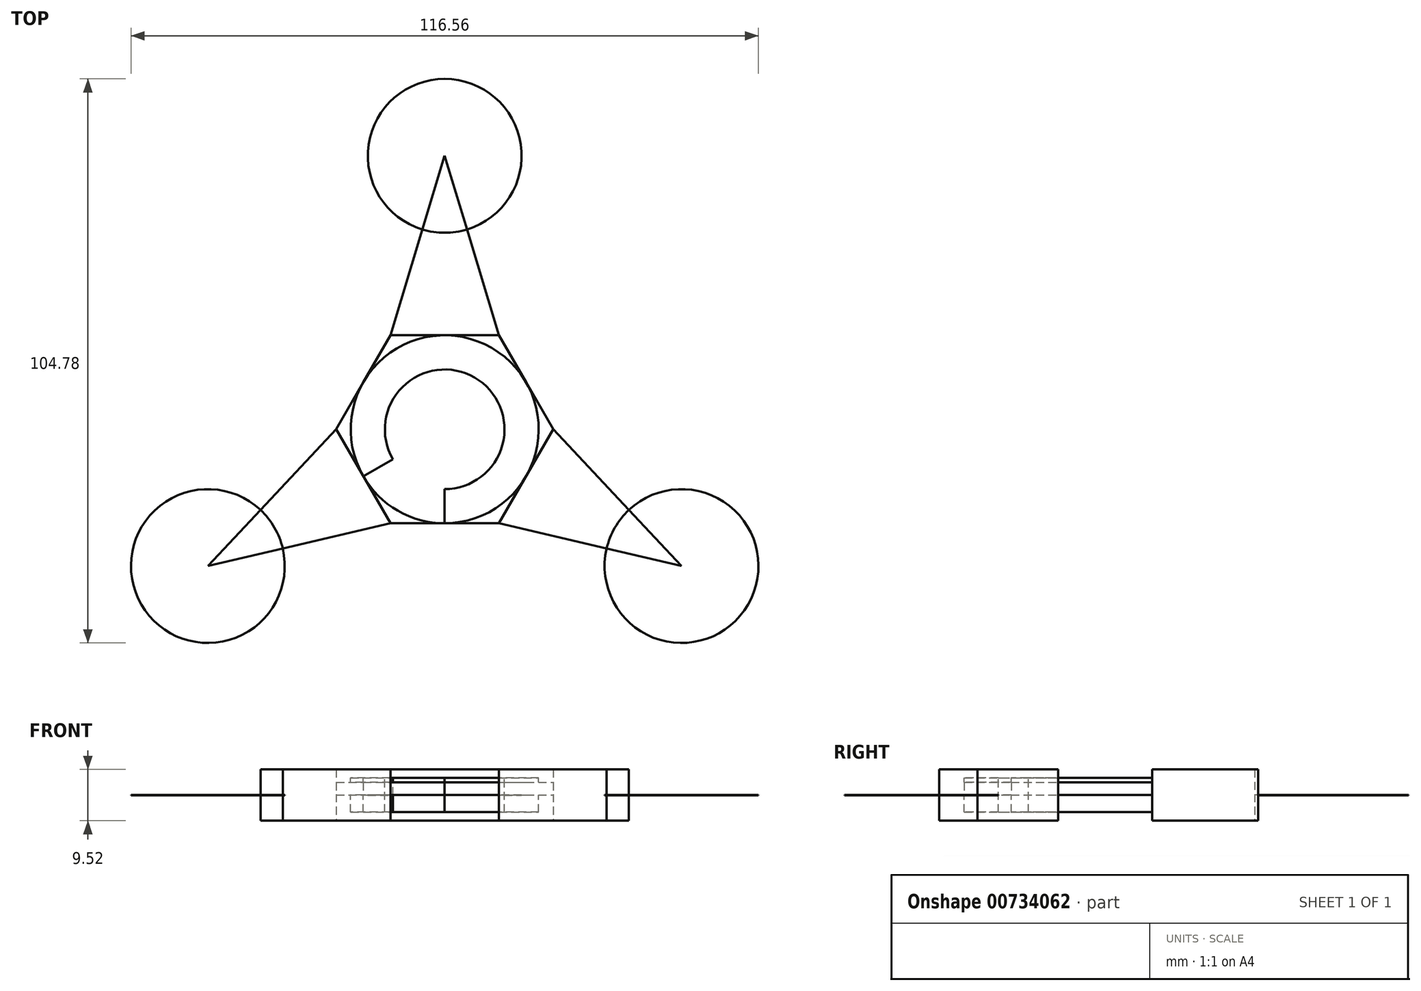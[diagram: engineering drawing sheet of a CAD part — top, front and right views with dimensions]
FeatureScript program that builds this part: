
annotation { "Feature Type Name" : "Feature", "Feature Type Description" : "" }
export const myFeature = defineFeature(function(context is Context, id is Id, definition is map)
    precondition{}
    {
        {
            var Q0;
            Q0=qCreatedBy(makeId("Top.planeOp"),FACE);
            var sketch = newSketch(context, id + "F0", { "sketchPlane" : qUnion([Q0])});
            skCircle(sketch, "E0", {"center": v(0, 0) * mm, "radius": 11.11 * mm});
            skCircle(sketch, "E1", {"center": v(0, 0) * mm, "radius": 17.46 * mm});
            skPoint(sketch, "E2.0.midPoint", {"position": v(15.12, 8.73) * mm});
            skCircle(sketch, "E3.cCircle", {"center": v(0, 0) * mm, "radius": 17.46 * mm, "construction": true});
            skLineSegment(sketch, "E3.0", {"start": v(10.08, 17.46) * mm, "end": v(20.16, 0) * mm});
            skLineSegment(sketch, "E3.1", {"start": v(20.16, 0) * mm, "end": v(10.08, -17.46) * mm});
            skLineSegment(sketch, "E3.2", {"start": v(10.08, -17.46) * mm, "end": v(-10.08, -17.46) * mm});
            skLineSegment(sketch, "E3.3", {"start": v(-10.08, -17.46) * mm, "end": v(-20.16, 0) * mm});
            skLineSegment(sketch, "E3.4", {"start": v(-20.16, 0) * mm, "end": v(-10.08, 17.46) * mm});
            skLineSegment(sketch, "E3.5", {"start": v(-10.08, 17.46) * mm, "end": v(10.08, 17.46) * mm});
            skLineSegment(sketch, "E4", {"start": v(-10.08, 17.46) * mm, "end": v(0, 50.8) * mm});
            skLineSegment(sketch, "E5", {"start": v(0, 50.8) * mm, "end": v(10.08, 17.46) * mm});
            skLineSegment(sketch, "E6", {"start": v(0, 50.8) * mm, "end": v(0, -50.8) * mm});
            skLineSegment(sketch, "E7", {"start": v(-20.16, 0) * mm, "end": v(-44, -25.4) * mm});
            skLineSegment(sketch, "E8", {"start": v(-44, -25.4) * mm, "end": v(-10.08, -17.46) * mm});
            skLineSegment(sketch, "E9", {"start": v(-44, -25.4) * mm, "end": v(44, 25.4) * mm});
            skLineSegment(sketch, "E10", {"start": v(10.08, -17.46) * mm, "end": v(44, -25.4) * mm});
            skLineSegment(sketch, "E11", {"start": v(44, -25.4) * mm, "end": v(20.16, 0) * mm});
            skLineSegment(sketch, "E12", {"start": v(44, -25.4) * mm, "end": v(-44, 25.4) * mm});
            skCircle(sketch, "E13", {"center": v(-44, -25.4) * mm, "radius": 14.29 * mm});
            skCircle(sketch, "E14", {"center": v(44, -25.4) * mm, "radius": 14.29 * mm});
            skCircle(sketch, "E15", {"center": v(0, 50.8) * mm, "radius": 14.29 * mm});
            skSolve(sketch);
        }
        {
            var Q0;
            {var subQ0=sQuery(id+"F0.wireOp",EDGE,"E9");var subQ1=sQuery(id+"F0.wireOp",EDGE,"E0");var subQ2=makeQuery(id+"F0.imprint","INTERSECT",VERTEX,{"disambiguationData":[OD(1.0)],"derivedFrom":[subQ1,subQ0]});Q0=makeQuery(id+"F0.imprint","IMPRINT",FACE,{"disambiguationData":[TD([[makeQuery(id+"F0.imprint","IMPRINT",EDGE,{"disambiguationData":[TD([[subQ2,-1.0]])],"derivedFrom":subQ1}),-1.0]])]});}
            var Q1;
            {var subQ0=sQuery(id+"F0.wireOp",EDGE,"E6");var subQ1=sQuery(id+"F0.wireOp",EDGE,"E0");var subQ2=makeQuery(id+"F0.imprint","INTERSECT",VERTEX,{"disambiguationData":[OD(0.0)],"derivedFrom":[subQ1,subQ0]});Q1=makeQuery(id+"F0.imprint","IMPRINT",FACE,{"disambiguationData":[TD([[makeQuery(id+"F0.imprint","IMPRINT",EDGE,{"disambiguationData":[TD([[subQ2,-1.0]])],"derivedFrom":subQ1}),-1.0]])]});}
            var Q2;
            {var subQ0=sQuery(id+"F0.wireOp",EDGE,"E12");var subQ1=sQuery(id+"F0.wireOp",EDGE,"E0");var subQ2=makeQuery(id+"F0.imprint","INTERSECT",VERTEX,{"disambiguationData":[OD(0.0)],"derivedFrom":[subQ1,subQ0]});Q2=makeQuery(id+"F0.imprint","IMPRINT",FACE,{"disambiguationData":[TD([[makeQuery(id+"F0.imprint","IMPRINT",EDGE,{"disambiguationData":[TD([[subQ2,-1.0]])],"derivedFrom":subQ1}),-1.0]])]});}
            var Q3;
            {var subQ0=sQuery(id+"F0.wireOp",EDGE,"E6");var subQ1=sQuery(id+"F0.wireOp",EDGE,"E0");var subQ2=makeQuery(id+"F0.imprint","INTERSECT",VERTEX,{"disambiguationData":[OD(0.0)],"derivedFrom":[subQ1,subQ0]});Q3=makeQuery(id+"F0.imprint","IMPRINT",FACE,{"disambiguationData":[TD([[makeQuery(id+"F0.imprint","IMPRINT",EDGE,{"disambiguationData":[TD([[subQ2,1.0]])],"derivedFrom":subQ1}),-1.0]])]});}
            var Q4;
            {var subQ0=sQuery(id+"F0.wireOp",EDGE,"E9");var subQ1=sQuery(id+"F0.wireOp",EDGE,"E0");var subQ2=makeQuery(id+"F0.imprint","INTERSECT",VERTEX,{"disambiguationData":[OD(0.0)],"derivedFrom":[subQ1,subQ0]});Q4=makeQuery(id+"F0.imprint","IMPRINT",FACE,{"disambiguationData":[TD([[makeQuery(id+"F0.imprint","IMPRINT",EDGE,{"disambiguationData":[TD([[subQ2,1.0]])],"derivedFrom":subQ1}),-1.0]])]});}
            var Q5;
            {var subQ0=sQuery(id+"F0.wireOp",EDGE,"E6");var subQ1=sQuery(id+"F0.wireOp",EDGE,"E0");var subQ2=makeQuery(id+"F0.imprint","INTERSECT",VERTEX,{"disambiguationData":[OD(1.0)],"derivedFrom":[subQ1,subQ0]});Q5=makeQuery(id+"F0.imprint","IMPRINT",FACE,{"disambiguationData":[TD([[makeQuery(id+"F0.imprint","IMPRINT",EDGE,{"disambiguationData":[TD([[subQ2,-1.0]])],"derivedFrom":subQ1}),-1.0]])]});}
            extrude(context, id + "F1", {"entities" : qUnion([Q0, Q1, Q2, Q3, Q4, Q5]), "oppositeDirection" : true, "depth" : 3.17 * mm, "offsetDistance" : 25.4 * mm, "hasSecondDirection" : true, "secondDirectionOppositeDirection" : false, "secondDirectionDepth" : 3.17 * mm});
        }
        {
            var Q0;
            {var subQ0=sQuery(id+"F0.wireOp",EDGE,"E3.4");var subQ1=sQuery(id+"F0.wireOp",EDGE,"E1");var subQ2=makeQuery(id+"F0.imprint","INTERSECT",VERTEX,{"derivedFrom":[subQ1,subQ0,sQuery(id+"F0.wireOp",EDGE,"E12")]});Q0=makeQuery(id+"F0.imprint","IMPRINT",FACE,{"disambiguationData":[TD([[makeQuery(id+"F0.imprint","IMPRINT",EDGE,{"disambiguationData":[TD([[subQ2,-1.0]])],"derivedFrom":subQ1}),-1.0]])]});}
            var Q1;
            {var subQ0=sQuery(id+"F0.wireOp",EDGE,"E3.2");var subQ1=sQuery(id+"F0.wireOp",EDGE,"E1");var subQ2=makeQuery(id+"F0.imprint","INTERSECT",VERTEX,{"derivedFrom":[subQ1,subQ0,sQuery(id+"F0.wireOp",EDGE,"E6")]});Q1=makeQuery(id+"F0.imprint","IMPRINT",FACE,{"disambiguationData":[TD([[makeQuery(id+"F0.imprint","IMPRINT",EDGE,{"disambiguationData":[TD([[subQ2,1.0]])],"derivedFrom":subQ1}),-1.0]])]});}
            var Q2;
            {var subQ0=sQuery(id+"F0.wireOp",EDGE,"E3.4");var subQ1=sQuery(id+"F0.wireOp",EDGE,"E1");var subQ2=makeQuery(id+"F0.imprint","INTERSECT",VERTEX,{"derivedFrom":[subQ1,subQ0,sQuery(id+"F0.wireOp",EDGE,"E12")]});Q2=makeQuery(id+"F0.imprint","IMPRINT",FACE,{"disambiguationData":[TD([[makeQuery(id+"F0.imprint","IMPRINT",EDGE,{"disambiguationData":[TD([[subQ2,1.0]])],"derivedFrom":subQ1}),-1.0]])]});}
            var Q3;
            {var subQ0=sQuery(id+"F0.wireOp",EDGE,"E3.0");var subQ1=sQuery(id+"F0.wireOp",EDGE,"E1");var subQ2=makeQuery(id+"F0.imprint","INTERSECT",VERTEX,{"derivedFrom":[subQ1,subQ0,sQuery(id+"F0.wireOp",EDGE,"E9")]});Q3=makeQuery(id+"F0.imprint","IMPRINT",FACE,{"disambiguationData":[TD([[makeQuery(id+"F0.imprint","IMPRINT",EDGE,{"disambiguationData":[TD([[subQ2,-1.0]])],"derivedFrom":subQ1}),-1.0]])]});}
            var Q4;
            {var subQ0=sQuery(id+"F0.wireOp",EDGE,"E3.2");var subQ1=sQuery(id+"F0.wireOp",EDGE,"E1");var subQ2=makeQuery(id+"F0.imprint","INTERSECT",VERTEX,{"derivedFrom":[subQ1,subQ0,sQuery(id+"F0.wireOp",EDGE,"E6")]});Q4=makeQuery(id+"F0.imprint","IMPRINT",FACE,{"disambiguationData":[TD([[makeQuery(id+"F0.imprint","IMPRINT",EDGE,{"disambiguationData":[TD([[subQ2,-1.0]])],"derivedFrom":subQ1}),-1.0]])]});}
            var Q5;
            {var subQ0=sQuery(id+"F0.wireOp",EDGE,"E3.0");var subQ1=sQuery(id+"F0.wireOp",EDGE,"E1");var subQ2=makeQuery(id+"F0.imprint","INTERSECT",VERTEX,{"derivedFrom":[subQ1,subQ0,sQuery(id+"F0.wireOp",EDGE,"E9")]});Q5=makeQuery(id+"F0.imprint","IMPRINT",FACE,{"disambiguationData":[TD([[makeQuery(id+"F0.imprint","IMPRINT",EDGE,{"disambiguationData":[TD([[subQ2,1.0]])],"derivedFrom":subQ1}),-1.0]])]});}
            extrude(context, id + "F2", {"entities" : qUnion([Q0, Q1, Q2, Q3, Q4, Q5]), "operationType" : NewBodyOperationType.ADD, "depth" : 2.38 * mm, "offsetDistance" : 25.4 * mm, "hasSecondDirection" : true, "secondDirectionOppositeDirection" : true, "secondDirectionDepth" : 3 / 812.8 * mm});
        }
        {
            var Q0;
            {var subQ0=sQuery(id+"F0.wireOp",EDGE,"E10");var subQ5=sQuery(id+"F0.wireOp",EDGE,"E14");var subQ6=makeQuery(id+"F0.imprint","INTERSECT",VERTEX,{"derivedFrom":[subQ0,subQ5]});Q0=makeQuery(id+"F0.imprint","IMPRINT",FACE,{"disambiguationData":[TD([[makeQuery(id+"F0.imprint","IMPRINT",EDGE,{"disambiguationData":[TD([[subQ6,1.0]])],"derivedFrom":subQ5}),-1.0]])]});}
            var Q1;
            {var subQ0=sQuery(id+"F0.wireOp",EDGE,"E11");var subQ5=sQuery(id+"F0.wireOp",EDGE,"E14");var subQ7=makeQuery(id+"F0.imprint","INTERSECT",VERTEX,{"derivedFrom":[subQ0,subQ5]});Q1=makeQuery(id+"F0.imprint","IMPRINT",FACE,{"disambiguationData":[TD([[makeQuery(id+"F0.imprint","IMPRINT",EDGE,{"disambiguationData":[TD([[subQ7,-1.0]])],"derivedFrom":subQ5}),-1.0]])]});}
            var Q2;
            {var subQ0=sQuery(id+"F0.wireOp",EDGE,"E5");var subQ5=sQuery(id+"F0.wireOp",EDGE,"E15");var subQ6=makeQuery(id+"F0.imprint","INTERSECT",VERTEX,{"derivedFrom":[subQ0,subQ5]});Q2=makeQuery(id+"F0.imprint","IMPRINT",FACE,{"disambiguationData":[TD([[makeQuery(id+"F0.imprint","IMPRINT",EDGE,{"disambiguationData":[TD([[subQ6,1.0]])],"derivedFrom":subQ5}),-1.0]])]});}
            var Q3;
            {var subQ0=sQuery(id+"F0.wireOp",EDGE,"E4");var subQ5=sQuery(id+"F0.wireOp",EDGE,"E15");var subQ6=makeQuery(id+"F0.imprint","INTERSECT",VERTEX,{"derivedFrom":[subQ0,subQ5]});Q3=makeQuery(id+"F0.imprint","IMPRINT",FACE,{"disambiguationData":[TD([[makeQuery(id+"F0.imprint","IMPRINT",EDGE,{"disambiguationData":[TD([[subQ6,-1.0]])],"derivedFrom":subQ5}),-1.0]])]});}
            var Q4;
            {var subQ0=sQuery(id+"F0.wireOp",EDGE,"E8");var subQ5=sQuery(id+"F0.wireOp",EDGE,"E13");var subQ6=makeQuery(id+"F0.imprint","INTERSECT",VERTEX,{"derivedFrom":[subQ0,subQ5]});Q4=makeQuery(id+"F0.imprint","IMPRINT",FACE,{"disambiguationData":[TD([[makeQuery(id+"F0.imprint","IMPRINT",EDGE,{"disambiguationData":[TD([[subQ6,-1.0]])],"derivedFrom":subQ5}),-1.0]])]});}
            var Q5;
            {var subQ0=sQuery(id+"F0.wireOp",EDGE,"E7");var subQ5=sQuery(id+"F0.wireOp",EDGE,"E13");var subQ6=makeQuery(id+"F0.imprint","INTERSECT",VERTEX,{"derivedFrom":[subQ0,subQ5]});Q5=makeQuery(id+"F0.imprint","IMPRINT",FACE,{"disambiguationData":[TD([[makeQuery(id+"F0.imprint","IMPRINT",EDGE,{"disambiguationData":[TD([[subQ6,1.0]])],"derivedFrom":subQ5}),-1.0]])]});}
            extrude(context, id + "F3", {"entities" : qUnion([Q0, Q1, Q2, Q3, Q4, Q5]), "surfaceOperationType" : NewSurfaceOperationType.ADD, "depth" : 4.76 * mm, "offsetDistance" : 25.4 * mm, "hasSecondDirection" : true, "secondDirectionOppositeDirection" : true, "secondDirectionDepth" : 4.76 * mm});
        }
        {
            var Q0;
            {var subQ1=sQuery(id+"F0.wireOp",EDGE,"E4");var subQ3=sQuery(id+"F0.wireOp",EDGE,"E15");var subQ4=makeQuery(id+"F0.imprint","INTERSECT",VERTEX,{"derivedFrom":[subQ1,subQ3]});Q0=makeQuery(id+"F0.imprint","IMPRINT",FACE,{"disambiguationData":[TD([[makeQuery(id+"F0.imprint","IMPRINT",EDGE,{"disambiguationData":[TD([[subQ4,1.0]])],"derivedFrom":subQ3}),1.0]])]});}
            var Q1;
            {var subQ1=sQuery(id+"F0.wireOp",EDGE,"E7");var subQ3=sQuery(id+"F0.wireOp",EDGE,"E13");var subQ4=makeQuery(id+"F0.imprint","INTERSECT",VERTEX,{"derivedFrom":[subQ1,subQ3]});Q1=makeQuery(id+"F0.imprint","IMPRINT",FACE,{"disambiguationData":[TD([[makeQuery(id+"F0.imprint","IMPRINT",EDGE,{"disambiguationData":[TD([[subQ4,-1.0]])],"derivedFrom":subQ3}),1.0]])]});}
            var Q2;
            {var subQ1=sQuery(id+"F0.wireOp",EDGE,"E10");var subQ3=sQuery(id+"F0.wireOp",EDGE,"E14");var subQ4=makeQuery(id+"F0.imprint","INTERSECT",VERTEX,{"derivedFrom":[subQ1,subQ3]});Q2=makeQuery(id+"F0.imprint","IMPRINT",FACE,{"disambiguationData":[TD([[makeQuery(id+"F0.imprint","IMPRINT",EDGE,{"disambiguationData":[TD([[subQ4,-1.0]])],"derivedFrom":subQ3}),1.0]])]});}
            extrude(context, id + "F4", {"entities" : qUnion([Q0, Q1, Q2]), "depth" : 5 / 812.8 * mm, "offsetDistance" : 25.4 * mm, "hasSecondDirection" : true, "secondDirectionOppositeDirection" : true, "secondDirectionDepth" : 5 / 812.8 * mm});
        }
        {
            var Q0;
            {var subQ1=sQuery(id+"F0.wireOp",EDGE,"E10");var subQ3=sQuery(id+"F0.wireOp",EDGE,"E14");var subQ4=makeQuery(id+"F0.imprint","INTERSECT",VERTEX,{"derivedFrom":[subQ1,subQ3]});Q0=makeQuery(id+"F0.imprint","IMPRINT",FACE,{"disambiguationData":[TD([[makeQuery(id+"F0.imprint","IMPRINT",EDGE,{"disambiguationData":[TD([[subQ4,1.0]])],"derivedFrom":subQ3}),1.0]])]});}
            var Q1;
            {var subQ1=sQuery(id+"F0.wireOp",EDGE,"E11");var subQ3=sQuery(id+"F0.wireOp",EDGE,"E14");var subQ4=makeQuery(id+"F0.imprint","INTERSECT",VERTEX,{"derivedFrom":[subQ1,subQ3]});Q1=makeQuery(id+"F0.imprint","IMPRINT",FACE,{"disambiguationData":[TD([[makeQuery(id+"F0.imprint","IMPRINT",EDGE,{"disambiguationData":[TD([[subQ4,-1.0]])],"derivedFrom":subQ3}),1.0]])]});}
            var Q2;
            {var subQ1=sQuery(id+"F0.wireOp",EDGE,"E5");var subQ3=sQuery(id+"F0.wireOp",EDGE,"E15");var subQ4=makeQuery(id+"F0.imprint","INTERSECT",VERTEX,{"derivedFrom":[subQ1,subQ3]});Q2=makeQuery(id+"F0.imprint","IMPRINT",FACE,{"disambiguationData":[TD([[makeQuery(id+"F0.imprint","IMPRINT",EDGE,{"disambiguationData":[TD([[subQ4,1.0]])],"derivedFrom":subQ3}),1.0]])]});}
            var Q3;
            {var subQ1=sQuery(id+"F0.wireOp",EDGE,"E4");var subQ3=sQuery(id+"F0.wireOp",EDGE,"E15");var subQ4=makeQuery(id+"F0.imprint","INTERSECT",VERTEX,{"derivedFrom":[subQ1,subQ3]});Q3=makeQuery(id+"F0.imprint","IMPRINT",FACE,{"disambiguationData":[TD([[makeQuery(id+"F0.imprint","IMPRINT",EDGE,{"disambiguationData":[TD([[subQ4,-1.0]])],"derivedFrom":subQ3}),1.0]])]});}
            var Q4;
            {var subQ1=sQuery(id+"F0.wireOp",EDGE,"E7");var subQ3=sQuery(id+"F0.wireOp",EDGE,"E13");var subQ4=makeQuery(id+"F0.imprint","INTERSECT",VERTEX,{"derivedFrom":[subQ1,subQ3]});Q4=makeQuery(id+"F0.imprint","IMPRINT",FACE,{"disambiguationData":[TD([[makeQuery(id+"F0.imprint","IMPRINT",EDGE,{"disambiguationData":[TD([[subQ4,1.0]])],"derivedFrom":subQ3}),1.0]])]});}
            var Q5;
            {var subQ1=sQuery(id+"F0.wireOp",EDGE,"E8");var subQ3=sQuery(id+"F0.wireOp",EDGE,"E13");var subQ4=makeQuery(id+"F0.imprint","INTERSECT",VERTEX,{"derivedFrom":[subQ1,subQ3]});Q5=makeQuery(id+"F0.imprint","IMPRINT",FACE,{"disambiguationData":[TD([[makeQuery(id+"F0.imprint","IMPRINT",EDGE,{"disambiguationData":[TD([[subQ4,-1.0]])],"derivedFrom":subQ3}),1.0]])]});}
            extrude(context, id + "F5", {"entities" : qUnion([Q0, Q1, Q2, Q3, Q4, Q5]), "depth" : 3 / 812.8 * mm, "offsetDistance" : 25.4 * mm, "hasSecondDirection" : true, "secondDirectionOppositeDirection" : true, "secondDirectionDepth" : 3 / 812.8 * mm});
        }
    });
